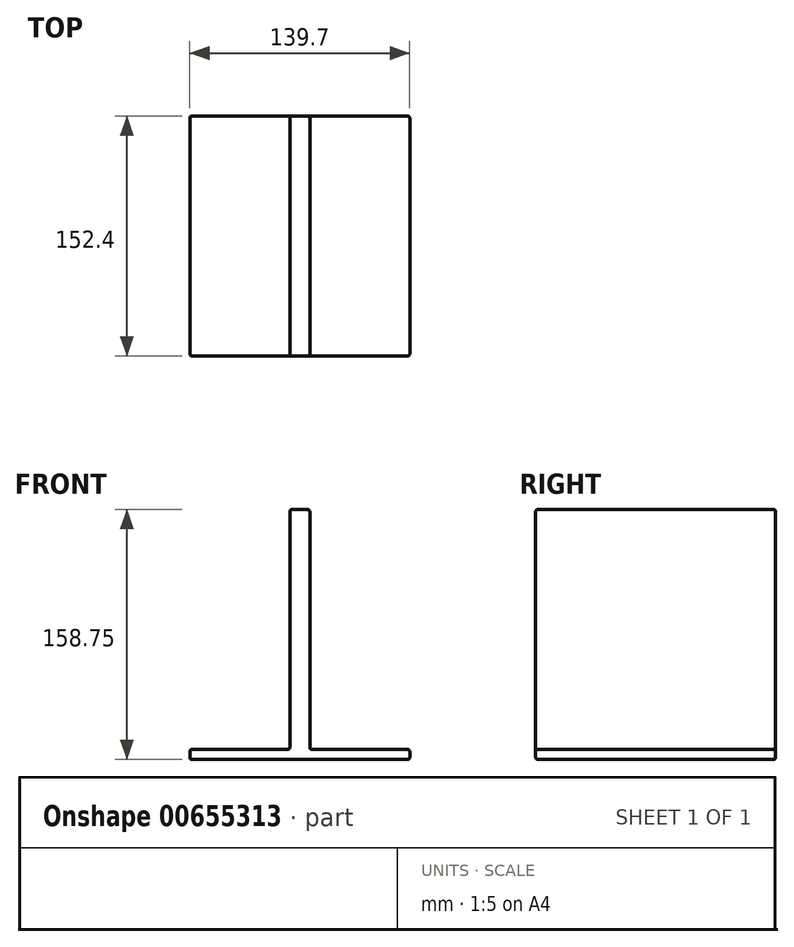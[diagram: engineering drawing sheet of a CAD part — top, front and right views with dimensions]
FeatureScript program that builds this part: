
annotation { "Feature Type Name" : "Feature", "Feature Type Description" : "" }
export const myFeature = defineFeature(function(context is Context, id is Id, definition is map)
    precondition{}
    {
        {
            var Q0;
            Q0=qCreatedBy(makeId("Front.planeOp"),FACE);
            var sketch = newSketch(context, id + "F0", { "sketchPlane" : qUnion([Q0])});
            skLineSegment(sketch, "E0", {"start": v(-103.07, -59.8) * mm, "end": v(36.63, -59.8) * mm});
            skLineSegment(sketch, "E1", {"start": v(36.63, -59.8) * mm, "end": v(36.63, -53.46) * mm});
            skLineSegment(sketch, "E2", {"start": v(-103.07, -59.8) * mm, "end": v(-103.07, -53.46) * mm});
            skLineSegment(sketch, "E3", {"start": v(-33.22, -59.8) * mm, "end": v(-33.22, 98.94) * mm, "construction": true});
            skLineSegment(sketch, "E4", {"start": v(36.63, -53.46) * mm, "end": v(-26.87, -53.46) * mm});
            skLineSegment(sketch, "E5", {"start": v(-103.07, -53.46) * mm, "end": v(-39.57, -53.46) * mm});
            skLineSegment(sketch, "E6", {"start": v(-26.87, -53.46) * mm, "end": v(-26.87, 98.94) * mm});
            skLineSegment(sketch, "E7", {"start": v(-39.57, -53.46) * mm, "end": v(-39.57, 98.94) * mm});
            skLineSegment(sketch, "E8", {"start": v(-39.57, 98.94) * mm, "end": v(-26.87, 98.94) * mm});
            skSolve(sketch);
        }
        {
            var Q0;
            Q0=makeQuery(id+"F0.imprint","IMPRINT",FACE,{"disambiguationData":[TD([[makeQuery(id+"F0.imprint","IMPRINT",EDGE,{"derivedFrom":sQuery(id+"F0.wireOp",EDGE,"E0")}),1.0]])]});
            extrude(context, id + "F1", {"entities" : qUnion([Q0]), "oppositeDirection" : true, "depth" : 152.4 * mm, "offsetDistance" : 25.4 * mm});
        }
        {
            var Q0;
            Q0=makeQuery(id+"F1.opExtrude","SWEPT_FACE",FACE,{"disambiguationData":[OSD([sQuery(id+"F0.wireOp",EDGE,"E1")])]});
            var Q1;
            Q1=makeQuery(id+"F1.opExtrude","CAP_FACE",FACE,{"disambiguationData":[OSD([sQuery(id+"F0.wireOp",EDGE,"E0"),sQuery(id+"F0.wireOp",EDGE,"E1"),sQuery(id+"F0.wireOp",EDGE,"E2"),sQuery(id+"F0.wireOp",EDGE,"E4"),sQuery(id+"F0.wireOp",EDGE,"E5"),sQuery(id+"F0.wireOp",EDGE,"E6"),sQuery(id+"F0.wireOp",EDGE,"E7"),sQuery(id+"F0.wireOp",EDGE,"E8")])],"isStart":true});
            var Q2;
            Q2=makeQuery(id+"F1.opExtrude","SWEPT_FACE",FACE,{"disambiguationData":[OSD([sQuery(id+"F0.wireOp",EDGE,"E4")])]});
            var Q3;
            Q3=makeQuery(id+"F1.opExtrude","SWEPT_FACE",FACE,{"disambiguationData":[OSD([sQuery(id+"F0.wireOp",EDGE,"E6")])]});
            var Q4;
            Q4=makeQuery(id+"F1.opExtrude","SWEPT_FACE",FACE,{"disambiguationData":[OSD([sQuery(id+"F0.wireOp",EDGE,"E8")])]});
            var Q5;
            Q5=makeQuery(id+"F1.opExtrude","SWEPT_FACE",FACE,{"disambiguationData":[OSD([sQuery(id+"F0.wireOp",EDGE,"E7")])]});
            var Q6;
            Q6=makeQuery(id+"F1.opExtrude","SWEPT_FACE",FACE,{"disambiguationData":[OSD([sQuery(id+"F0.wireOp",EDGE,"E5")])]});
            var Q7;
            Q7=makeQuery(id+"F1.opExtrude","SWEPT_FACE",FACE,{"disambiguationData":[OSD([sQuery(id+"F0.wireOp",EDGE,"E2")])]});
            var Q8;
            Q8=makeQuery(id+"F1.opExtrude","CAP_FACE",FACE,{"disambiguationData":[OSD([sQuery(id+"F0.wireOp",EDGE,"E0"),sQuery(id+"F0.wireOp",EDGE,"E1"),sQuery(id+"F0.wireOp",EDGE,"E2"),sQuery(id+"F0.wireOp",EDGE,"E4"),sQuery(id+"F0.wireOp",EDGE,"E5"),sQuery(id+"F0.wireOp",EDGE,"E6"),sQuery(id+"F0.wireOp",EDGE,"E7"),sQuery(id+"F0.wireOp",EDGE,"E8")])],"isStart":false});
            fillet(context, id + "F2", {"entities" : qUnion([Q0, Q1, Q2, Q3, Q4, Q5, Q6, Q7, Q8]), "radius" : 1.27 * mm, "tangentPropagation" : true, "allowEdgeOverflow" : false});
        }
    });
